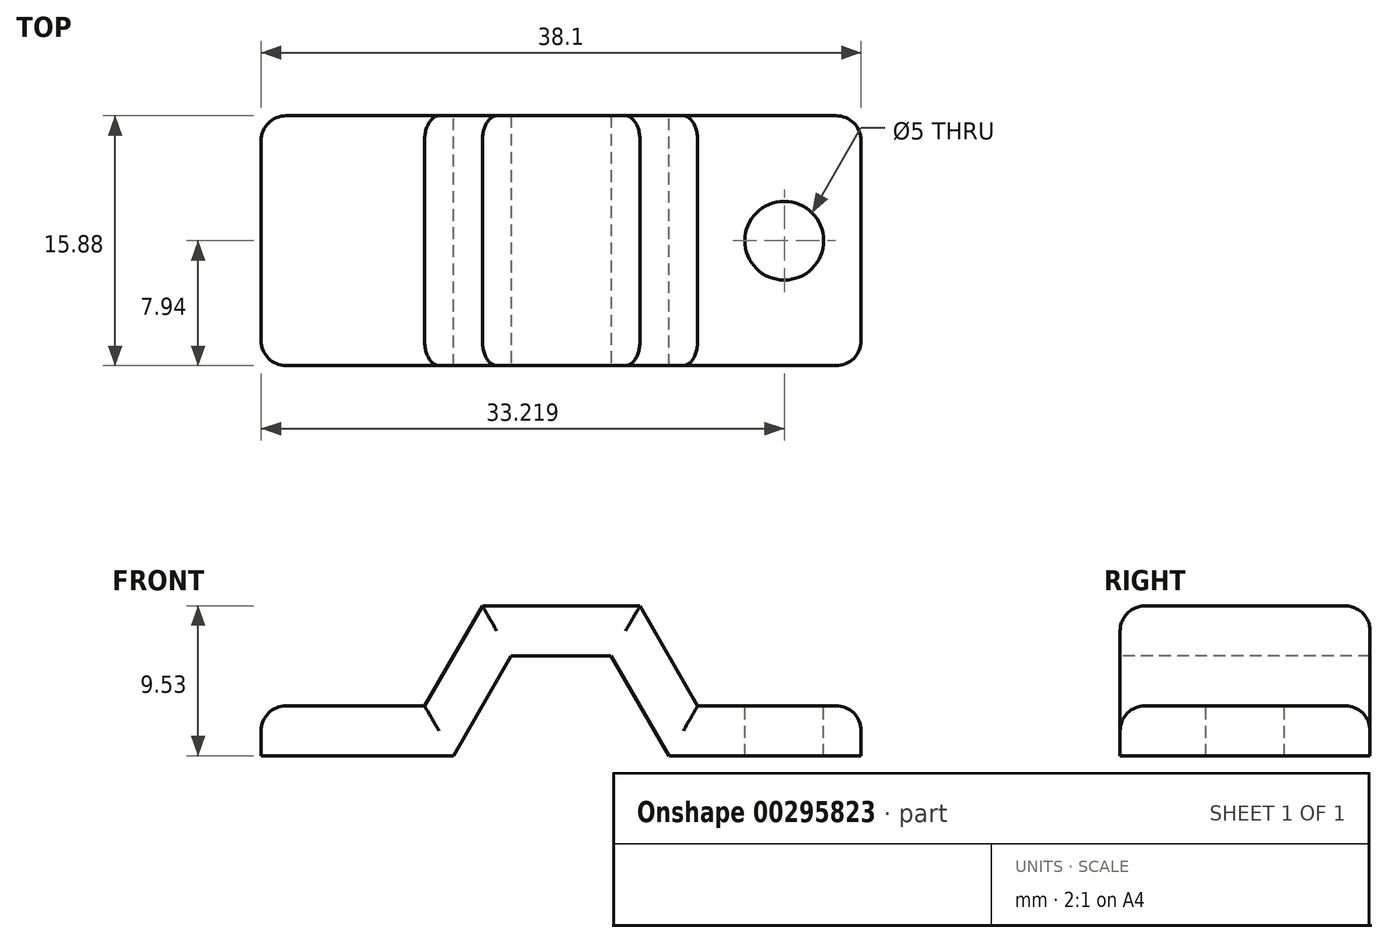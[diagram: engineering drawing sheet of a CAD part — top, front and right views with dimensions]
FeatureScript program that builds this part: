
annotation { "Feature Type Name" : "Feature", "Feature Type Description" : "" }
export const myFeature = defineFeature(function(context is Context, id is Id, definition is map)
    precondition{}
    {
        {
            var Q0;
            Q0=qCreatedBy(makeId("Front.planeOp"),FACE);
            var sketch = newSketch(context, id + "F0", { "sketchPlane" : qUnion([Q0])});
            skLineSegment(sketch, "E0", {"start": v(0, 0) * mm, "end": v(0, 6.35) * mm, "construction": true});
            skLineSegment(sketch, "E1", {"start": v(0, 6.35) * mm, "end": v(-3.17, 6.35) * mm});
            skLineSegment(sketch, "E2", {"start": v(-3.17, 6.35) * mm, "end": v(-6.84, 0) * mm});
            skLineSegment(sketch, "E3", {"start": v(-6.84, 0) * mm, "end": v(-19.05, 0) * mm});
            skLineSegment(sketch, "E4.MirrorCS", {"start": v(0, 6.35) * mm, "end": v(3.17, 6.35) * mm});
            skLineSegment(sketch, "E5.MirrorCS", {"start": v(3.17, 6.35) * mm, "end": v(6.84, 0) * mm});
            skLineSegment(sketch, "E6.MirrorCS", {"start": v(6.84, 0) * mm, "end": v(19.05, 0) * mm});
            skSolve(sketch);
        }
        {
            var Q0;
            Q0=sQuery(id+"F0.wireOp",VERTEX,"E3.end");
            var Q1;
            Q1=sQuery(id+"F0.wireOp",EDGE,"E3");
            cPlane(context, id + "F1", {"entities" : qUnion([Q0, Q1]), "cplaneType" : CPlaneType.LINE_POINT, "offset" : 25.4 * mm, "width" : 152.4 * mm, "height" : 152.4 * mm});
        }
        {
            var Q0;
            Q0=qCreatedBy(id+"F1.planeOp",FACE);
            var sketch = newSketch(context, id + "F2", { "sketchPlane" : qUnion([Q0])});
            skLineSegment(sketch, "E7.bottom", {"start": v(7.94, 0) * mm, "end": v(-7.94, 0) * mm});
            skLineSegment(sketch, "E7.top", {"start": v(6.35, 3.18) * mm, "end": v(-6.35, 3.18) * mm});
            skLineSegment(sketch, "E7.left", {"start": v(7.94, 0) * mm, "end": v(7.94, 1.59) * mm});
            skLineSegment(sketch, "E7.right", {"start": v(-7.94, 0) * mm, "end": v(-7.94, 1.59) * mm});
            skPoint(sketch, "E8.visualSharp", {"position": v(7.94, 3.18) * mm});
            skArc(sketch, "E8.filletArc", {"start": v(7.94, 1.59) * mm, "mid": v(7.47, 2.71) * mm, "end": v(6.35, 3.18) * mm});
            skPoint(sketch, "E9.visualSharp", {"position": v(-7.94, 3.18) * mm});
            skArc(sketch, "E9.filletArc", {"start": v(-6.35, 3.18) * mm, "mid": v(-7.47, 2.71) * mm, "end": v(-7.94, 1.59) * mm});
            skSolve(sketch);
        }
        {
            var Q0;
            Q0=makeQuery(id+"F2.imprint","IMPRINT",FACE,{"disambiguationData":[TD([[makeQuery(id+"F2.imprint","IMPRINT",EDGE,{"derivedFrom":sQuery(id+"F2.wireOp",EDGE,"E7.bottom")}),-1.0]])]});
            var Q1;
            Q1=sQuery(id+"F0.wireOp",EDGE,"E3");
            var Q2;
            Q2=sQuery(id+"F0.wireOp",EDGE,"E2");
            var Q3;
            Q3=sQuery(id+"F0.wireOp",EDGE,"E1");
            var Q4;
            Q4=sQuery(id+"F0.wireOp",EDGE,"E5.MirrorCS");
            var Q5;
            Q5=sQuery(id+"F0.wireOp",EDGE,"E4.MirrorCS");
            var Q6;
            Q6=sQuery(id+"F0.wireOp",EDGE,"E6.MirrorCS");
            sweep(context, id + "F3", {"profiles" : qUnion([Q0]), "path" : qUnion([Q1, Q2, Q3, Q4, Q5, Q6])});
        }
        {
            var Q0;
            Q0=makeQuery(id+"F3.opSweep","SWEPT_FACE",FACE,{"disambiguationData":[OSD([sQuery(id+"F0.wireOp",EDGE,"E3"),sQuery(id+"F2.wireOp",EDGE,"E7.top")])]});
            var sketch = newSketch(context, id + "F4", { "sketchPlane" : qUnion([Q0])});
            skCircle(sketch, "E10", {"center": v(-14.17, 0) * mm, "radius": 2.5 * mm});
            skPoint(sketch, "E10.centerSnap0", {"position": v(-19.05, 0) * mm});
            skCircle(sketch, "E11.MirrorC", {"center": v(14.17, 0) * mm, "radius": 2.5 * mm});
            skSolve(sketch);
        }
        {
            var Q0;
            Q0=makeQuery(id+"F4.imprint","IMPRINT",FACE,{"disambiguationData":[TD([[makeQuery(id+"F4.imprint","IMPRINT",EDGE,{"derivedFrom":sQuery(id+"F4.wireOp",EDGE,"E10")}),-1.0]])]});
            var Q1;
            Q1=makeQuery(id+"F4.imprint","IMPRINT",FACE,{"disambiguationData":[TD([[makeQuery(id+"F4.imprint","IMPRINT",EDGE,{"derivedFrom":sQuery(id+"F4.wireOp",EDGE,"E11.MirrorC")}),1.0]])]});
            extrude(context, id + "F5", {"entities" : qUnion([Q0, Q1]), "operationType" : NewBodyOperationType.REMOVE, "endBound" : BoundingType.UP_TO_NEXT, "oppositeDirection" : true, "depth" : 25.4 * mm});
        }
        {
            var Q0;
            Q0=makeQuery(id+"F3.opSweep","CAP_EDGE",EDGE,{"disambiguationData":[OSD([sQuery(id+"F0.wireOp",VERTEX,"E3.end"),sQuery(id+"F2.wireOp",EDGE,"E7.top")])],"isStart":true});
            var Q1;
            Q1=makeQuery(id+"F3.opSweep","CAP_EDGE",EDGE,{"disambiguationData":[OSD([sQuery(id+"F0.wireOp",VERTEX,"E6.MirrorCS.end"),sQuery(id+"F2.wireOp",EDGE,"E7.top")])],"isStart":false});
            fillet(context, id + "F6", {"entities" : qUnion([Q0, Q1]), "radius" : 1.59 * mm, "tangentPropagation" : true, "allowEdgeOverflow" : false});
        }
    });
